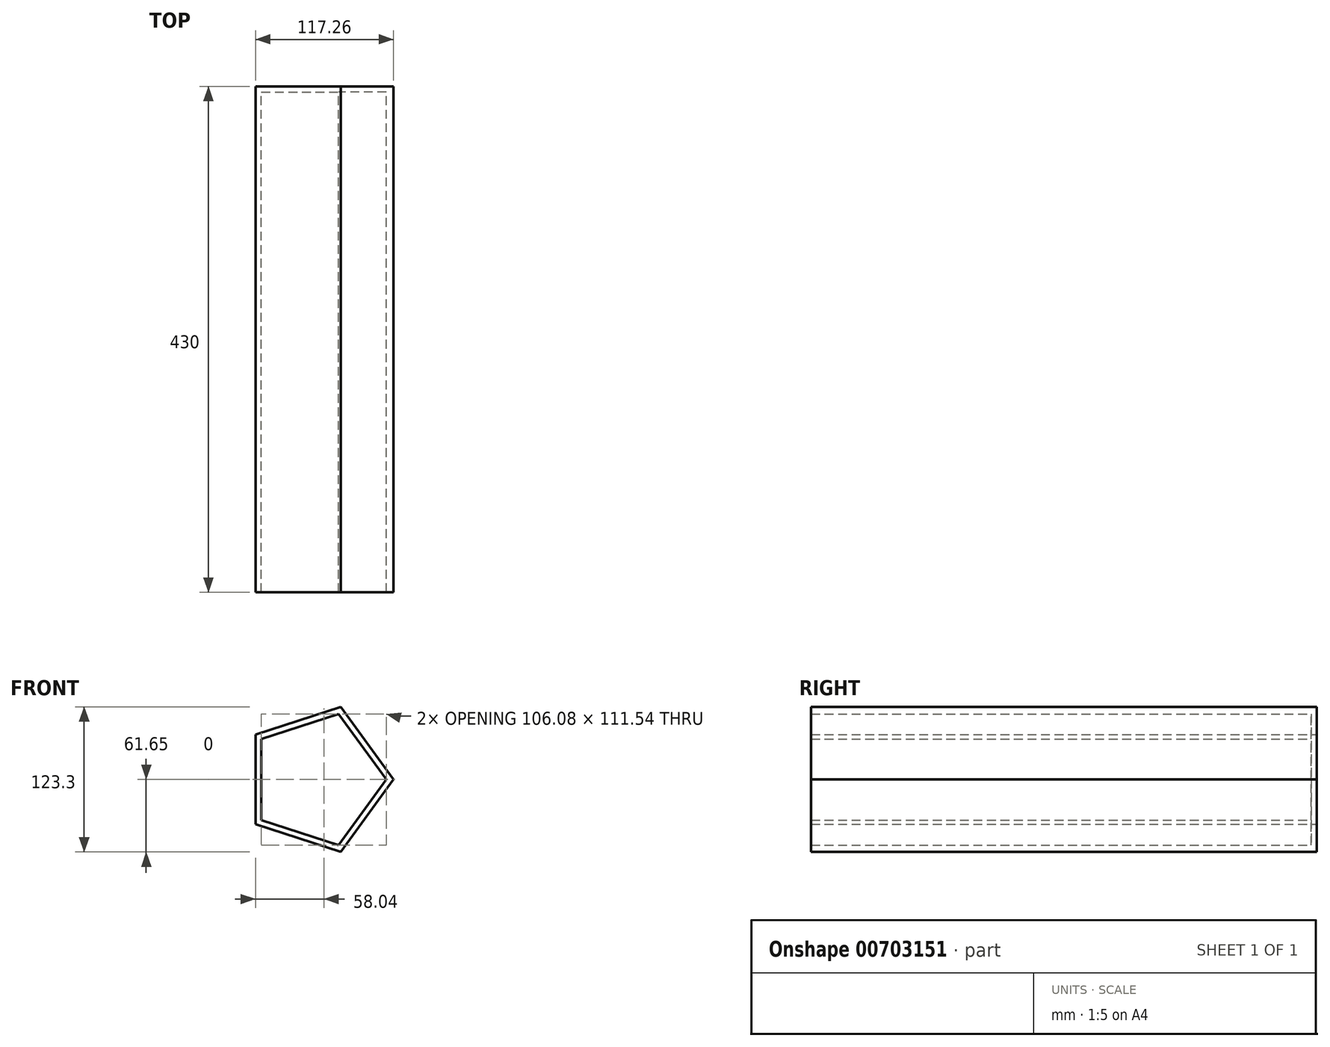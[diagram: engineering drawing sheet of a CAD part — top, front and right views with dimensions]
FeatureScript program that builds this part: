
annotation { "Feature Type Name" : "Feature", "Feature Type Description" : "" }
export const myFeature = defineFeature(function(context is Context, id is Id, definition is map)
    precondition{}
    {
        {
            var Q0;
            Q0=qCreatedBy(makeId("Front.planeOp"),FACE);
            var sketch = newSketch(context, id + "F0", { "sketchPlane" : qUnion([Q0])});
            skCircle(sketch, "E0.cCircle", {"center": v(0, 0) * mm, "radius": 64.82 * mm, "construction": true});
            skLineSegment(sketch, "E0.0", {"start": v(64.82, 0) * mm, "end": v(20.03, -61.65) * mm});
            skLineSegment(sketch, "E0.1", {"start": v(20.03, -61.65) * mm, "end": v(-52.44, -38.1) * mm});
            skLineSegment(sketch, "E0.2", {"start": v(-52.44, -38.1) * mm, "end": v(-52.44, 38.1) * mm});
            skLineSegment(sketch, "E0.3", {"start": v(-52.44, 38.1) * mm, "end": v(20.03, 61.65) * mm});
            skLineSegment(sketch, "E0.4", {"start": v(20.03, 61.65) * mm, "end": v(64.82, 0) * mm});
            skSolve(sketch);
        }
        {
            var Q0;
            Q0=makeQuery(id+"F0.imprint","IMPRINT",FACE,{"disambiguationData":[TD([[makeQuery(id+"F0.imprint","IMPRINT",EDGE,{"derivedFrom":sQuery(id+"F0.wireOp",EDGE,"E0.0")}),-1.0]])]});
            extrude(context, id + "F1", {"entities" : qUnion([Q0]), "depth" : 430 * mm, "offsetDistance" : 25 * mm});
        }
        {
            var Q0;
            Q0=makeQuery(id+"F1.opExtrude","CAP_FACE",FACE,{"disambiguationData":[OSD([sQuery(id+"F0.wireOp",EDGE,"E0.0"),sQuery(id+"F0.wireOp",EDGE,"E0.1"),sQuery(id+"F0.wireOp",EDGE,"E0.2"),sQuery(id+"F0.wireOp",EDGE,"E0.3"),sQuery(id+"F0.wireOp",EDGE,"E0.4")])],"isStart":false});
            shell(context, id + "F2", {"entities" : qUnion([Q0]), "thickness" : 5 * mm});
        }
    });
